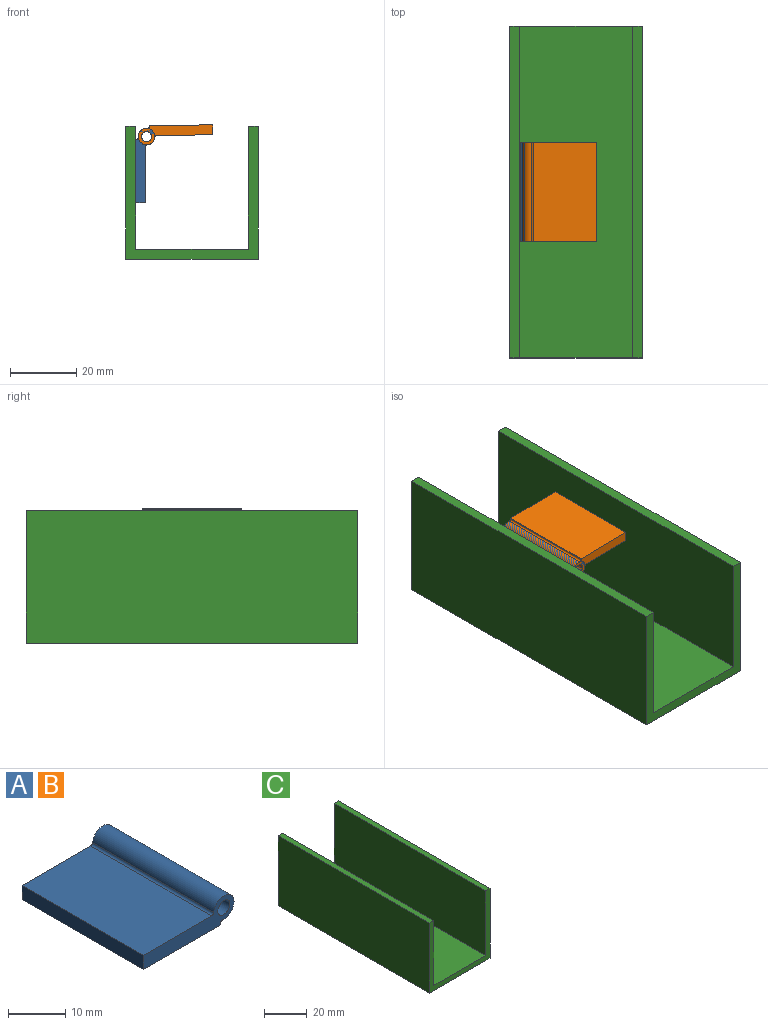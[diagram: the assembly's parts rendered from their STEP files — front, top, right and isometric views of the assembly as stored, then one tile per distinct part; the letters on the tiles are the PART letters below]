
ASSEMBLY  parts=3 mates=2
PART A: 10 faces, bbox 22.5x30x5.8 mm
  f0: plane 30x3mm, normal (-1,0,0), area 90mm2, adj f1,f7,f8,f9
  f1: plane 30x19.1mm, normal (0,0,-1), area 573mm2, adj f0,f2,f8,f9
  f2: plane 30x0.33mm, normal (1,0,0), area 9.8mm2, adj f1,f3,f8,f9
  f3: cylinder r=0.5mm len=30mm, axis (0,1,0), area 25.6mm2, adj f2,f4,f8,f9
  f4: cylinder r=2.5mm len=30mm, axis (0,1,0), area 358.5mm2, adj f3,f5,f8,f9
  f5: cylinder r=0.5mm len=30mm, axis (0,1,0), area 22.6mm2, adj f4,f7,f8,f9
  f6: cylinder r=1.5mm len=30mm, axis (0,1,0), area 282.7mm2, adj f8,f9
  f7: plane 30x17.01mm, normal (0,0,1), area 510.2mm2, adj f0,f5,f8,f9
  f8: plane 22.5x5.8mm, normal (0,-1,0), area 67.8mm2, adj f0,f1,f2,f3,f4,f5,f6,f7
  f9: plane 22.5x5.8mm, normal (0,1,0), area 67.8mm2, adj f0,f1,f2,f3,f4,f5,f6,f7
PART B: same geometry as A
PART C: 10 faces, bbox 40x100x40 mm
  f0: plane 100x3mm, normal (0,0,1), area 300mm2, adj f1,f7,f8,f9
  f1: plane 100x40mm, normal (-1,0,0), area 4000mm2, adj f0,f2,f8,f9
  f2: plane 100x40mm, normal (0,0,-1), area 4000mm2, adj f1,f3,f8,f9
  f3: plane 100x40mm, normal (1,0,0), area 4000mm2, adj f2,f4,f8,f9
  f4: plane 100x3mm, normal (0,0,1), area 300mm2, adj f3,f5,f8,f9
  f5: plane 100x37mm, normal (-1,0,0), area 3700mm2, adj f4,f6,f8,f9
  f6: plane 100x34mm, normal (0,0,1), area 3400mm2, adj f5,f7,f8,f9
  f7: plane 100x37mm, normal (1,0,0), area 3700mm2, adj f0,f6,f8,f9
  f8: plane 40x40mm, normal (0,-1,0), area 342mm2, adj f0,f1,f2,f3,f4,f5,f6,f7
  f9: plane 40x40mm, normal (0,1,0), area 342mm2, adj f0,f1,f2,f3,f4,f5,f6,f7
PLACE A rot(axis=(-0.71,0,-0.71),180deg) t=(-47.05,-13.68,-21.25)mm
PLACE B rot(axis=(0,1,0),179.3deg) t=(-23.79,16.32,2.29)mm
PLACE C t=(-50.05,51.32,-38.2)mm
MATE revolute B.f4 <-> A.f4  axis (0,-1,0) through (-43.75,-13.68,-1.25)mm
MATE fastened C.f7 <-> A.f1  axis (1,0,0) through (-47.05,1.32,-16.7)mm
